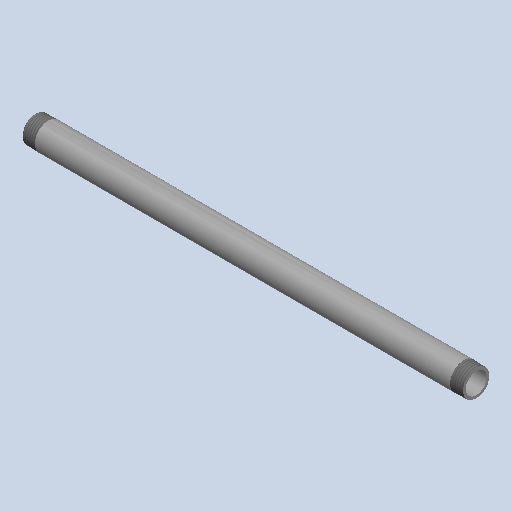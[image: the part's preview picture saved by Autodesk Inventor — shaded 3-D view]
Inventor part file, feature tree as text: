
AUTODESK INVENTOR PART (.ipt)
format: ipt  version: 2025 (Build 290162000, 162)  size: 164,864 bytes
history: native  units: mm (DEFAULTED — no unit token found)
features: other x8, revolve x1
ambient origin geometry x8: Origin, YZ Plane, XZ Plane, XY Plane, X Axis, Y Axis, Z Axis, Center Point
bodies: Solid1 (feature_tree)
feature tree (9):
  revolve  "Revolution1"  [1 undecoded]
  other  "Work Axis1"
  other  "Work Point5"
  other  "Work Axis2"
  other  "Work Point6"
  other  "Work Axis3"
  other  "Work Axis4"
  other  "Work Point7"
  other  "Work Point8"
note: 1 required parameter value undecoded (feature->parameter linkage not recoverable at this tier; creation-order binding heuristic only, values carry confidence <= 0.55)
